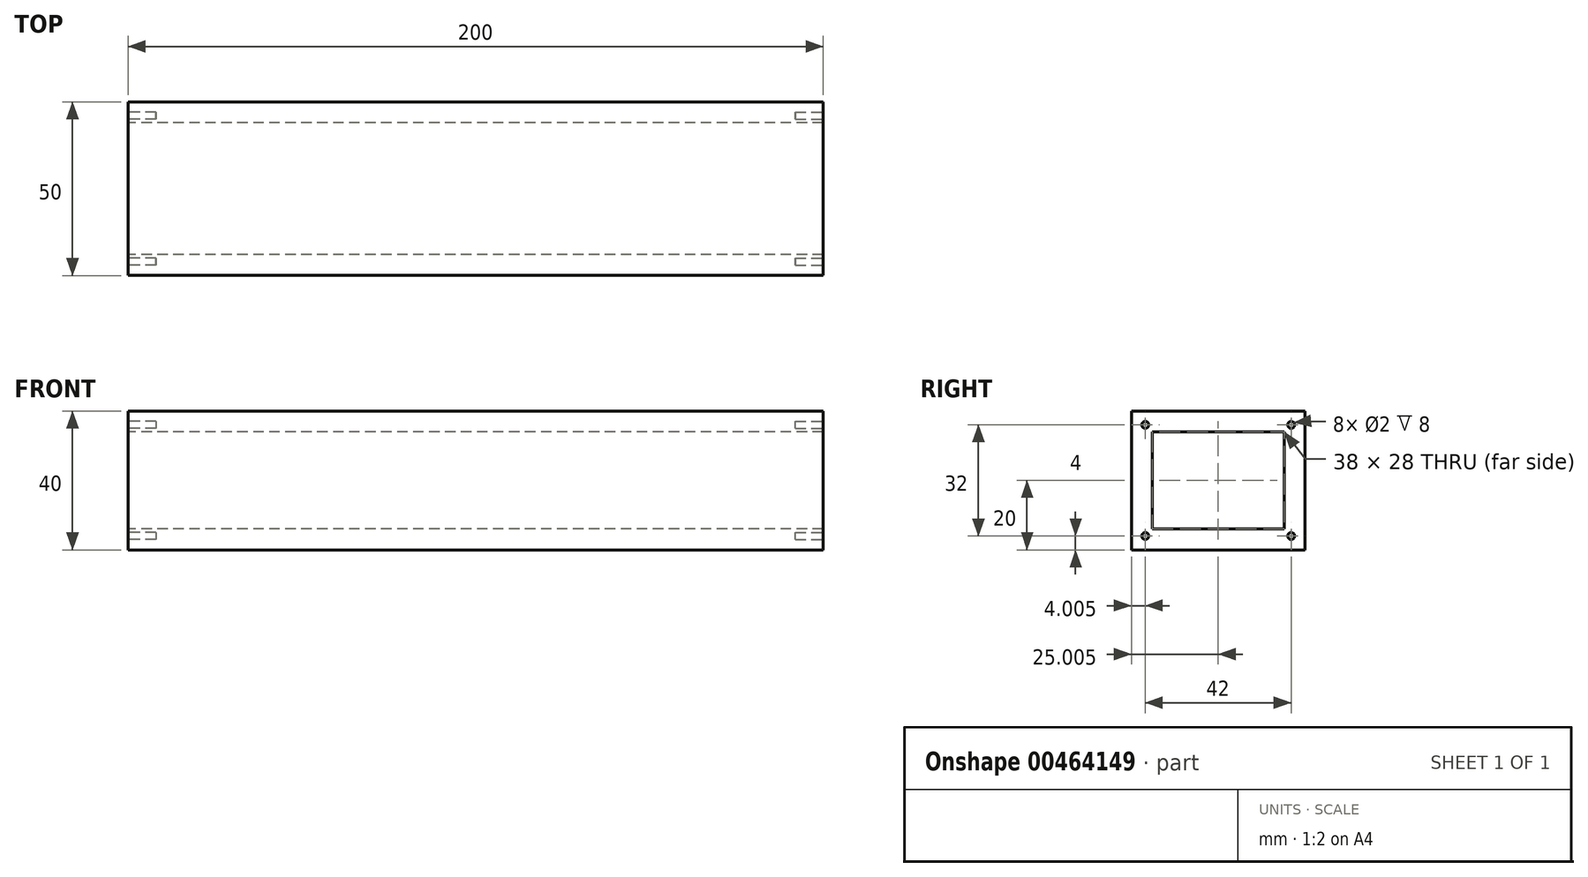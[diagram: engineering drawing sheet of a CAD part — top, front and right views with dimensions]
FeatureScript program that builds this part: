
annotation { "Feature Type Name" : "Feature", "Feature Type Description" : "" }
export const myFeature = defineFeature(function(context is Context, id is Id, definition is map)
    precondition{}
    {
        {
            var Q0;
            Q0=qCreatedBy(makeId("Top.planeOp"),FACE);
            var sketch = newSketch(context, id + "F0", { "sketchPlane" : qUnion([Q0])});
            skLineSegment(sketch, "E0.bottom", {"start": v(-59.16, -4.12) * mm, "end": v(140.84, -4.12) * mm});
            skLineSegment(sketch, "E0.top", {"start": v(-59.16, -54.12) * mm, "end": v(140.84, -54.12) * mm});
            skLineSegment(sketch, "E0.left", {"start": v(-59.16, -4.12) * mm, "end": v(-59.16, -54.12) * mm});
            skLineSegment(sketch, "E0.right", {"start": v(140.84, -4.12) * mm, "end": v(140.84, -54.12) * mm});
            skSolve(sketch);
        }
        {
            var Q0;
            Q0 = qSketchRegion(id + "F0", true);
            extrude(context, id + "F1", {"entities" : qUnion([Q0]), "depth" : 40 * mm, "offsetDistance" : 25 * mm});
        }
        {
            var Q0;
            Q0=makeQuery(id+"F1.opExtrude","SWEPT_FACE",FACE,{"disambiguationData":[OSD([sQuery(id+"F0.wireOp",EDGE,"E0.left")])]});
            var sketch = newSketch(context, id + "F2", { "sketchPlane" : qUnion([Q0])});
            skLineSegment(sketch, "E1.bottom", {"start": v(10.12, 34) * mm, "end": v(48.12, 34) * mm});
            skLineSegment(sketch, "E1.top", {"start": v(10.12, 6) * mm, "end": v(48.12, 6) * mm});
            skLineSegment(sketch, "E1.left", {"start": v(10.12, 34) * mm, "end": v(10.12, 6) * mm});
            skLineSegment(sketch, "E1.right", {"start": v(48.12, 34) * mm, "end": v(48.12, 6) * mm});
            skSolve(sketch);
        }
        {
            var Q0;
            Q0 = qSketchRegion(id + "F2", true);
            extrude(context, id + "F3", {"entities" : qUnion([Q0]), "operationType" : NewBodyOperationType.REMOVE, "endBound" : BoundingType.THROUGH_ALL, "oppositeDirection" : true, "depth" : 25 * mm});
        }
        {
            var Q0;
            Q0=makeQuery(id+"F1.opExtrude","SWEPT_FACE",FACE,{"disambiguationData":[OSD([sQuery(id+"F0.wireOp",EDGE,"E0.left")])]});
            var sketch = newSketch(context, id + "F4", { "sketchPlane" : qUnion([Q0])});
            skCircle(sketch, "E2", {"center": v(8.12, 36) * mm, "radius": 1 * mm});
            skCircle(sketch, "E3", {"center": v(8.12, 4) * mm, "radius": 1 * mm});
            skCircle(sketch, "E4", {"center": v(50.12, 4) * mm, "radius": 1 * mm});
            skCircle(sketch, "E5", {"center": v(50.12, 36) * mm, "radius": 1 * mm});
            skSolve(sketch);
        }
        {
            var Q0;
            Q0 = qSketchRegion(id + "F4", true);
            extrude(context, id + "F5", {"entities" : qUnion([Q0]), "operationType" : NewBodyOperationType.REMOVE, "oppositeDirection" : true, "depth" : 8 * mm});
        }
        {
            var Q0;
            Q0=makeQuery(id+"F1.opExtrude","SWEPT_FACE",FACE,{"disambiguationData":[OSD([sQuery(id+"F0.wireOp",EDGE,"E0.right")])]});
            var sketch = newSketch(context, id + "F6", { "sketchPlane" : qUnion([Q0])});
            skCircle(sketch, "E6", {"center": v(-50.12, 36) * mm, "radius": 1 * mm});
            skCircle(sketch, "E7", {"center": v(-8.12, 36) * mm, "radius": 1 * mm});
            skCircle(sketch, "E8", {"center": v(-8.12, 4) * mm, "radius": 1 * mm});
            skCircle(sketch, "E9", {"center": v(-50.12, 4) * mm, "radius": 1 * mm});
            skSolve(sketch);
        }
        {
            var Q0;
            Q0 = qSketchRegion(id + "F6", true);
            extrude(context, id + "F7", {"entities" : qUnion([Q0]), "operationType" : NewBodyOperationType.REMOVE, "oppositeDirection" : true, "depth" : 8 * mm});
        }
    });
